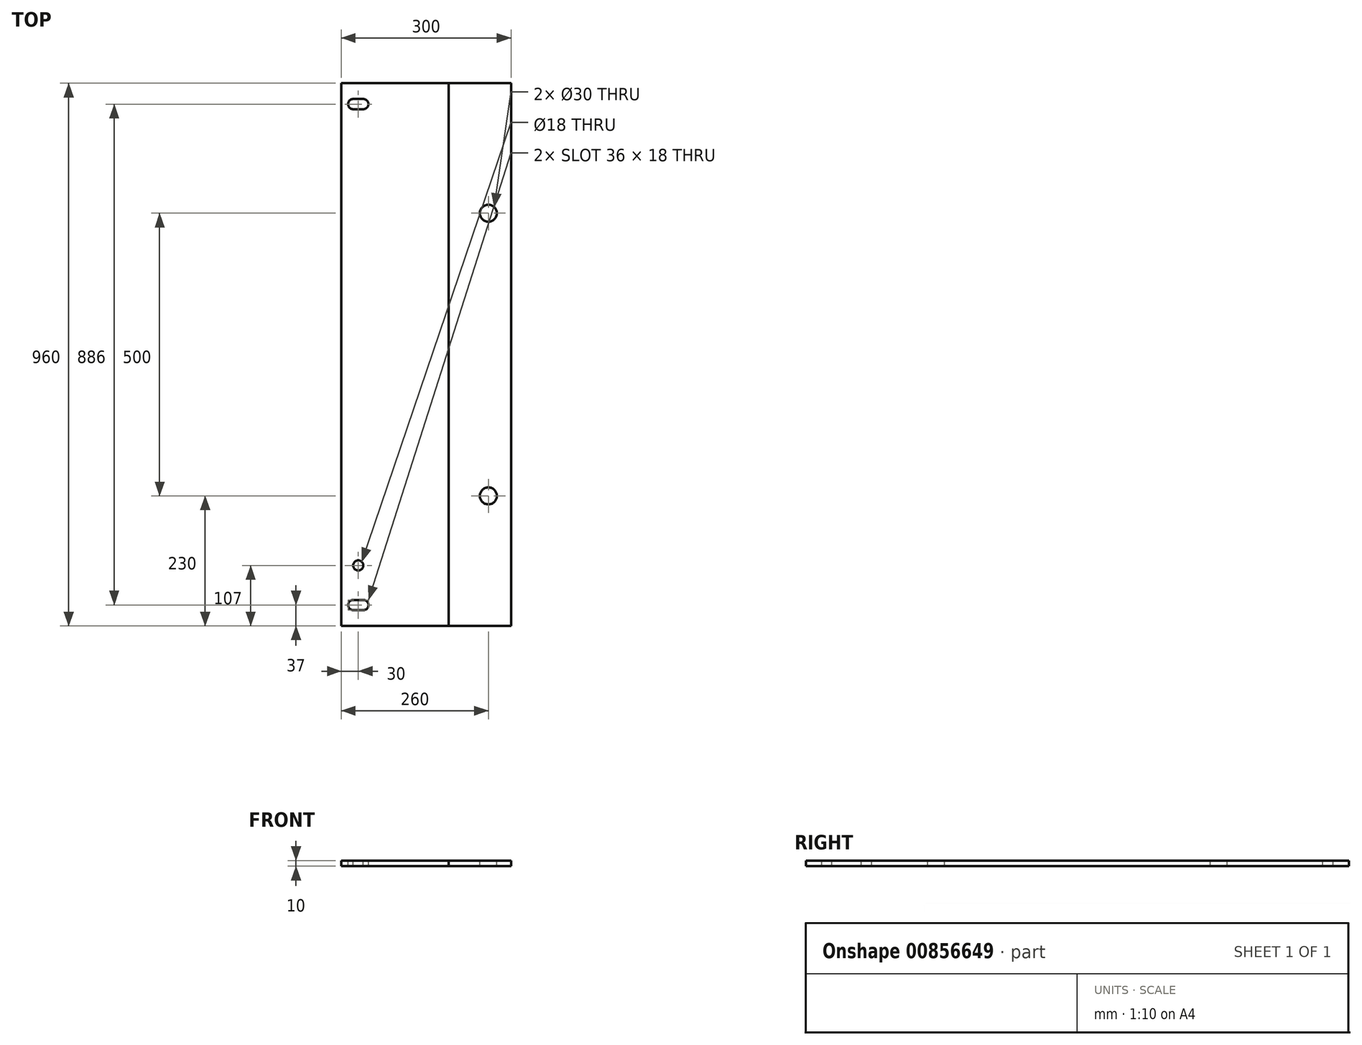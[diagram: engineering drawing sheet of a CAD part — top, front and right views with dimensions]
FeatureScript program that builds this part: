
annotation { "Feature Type Name" : "Feature", "Feature Type Description" : "" }
export const myFeature = defineFeature(function(context is Context, id is Id, definition is map)
    precondition{}
    {
        {
            var Q0;
            Q0=qCreatedBy(makeId("Top.planeOp"),FACE);
            var sketch = newSketch(context, id + "F0", { "sketchPlane" : qUnion([Q0])});
            skLineSegment(sketch, "E0.bottom", {"start": v(95, 480) * mm, "end": v(-95, 480) * mm});
            skLineSegment(sketch, "E0.top", {"start": v(95, -480) * mm, "end": v(-95, -480) * mm});
            skLineSegment(sketch, "E0.left", {"start": v(95, 480) * mm, "end": v(95, -480) * mm});
            skLineSegment(sketch, "E0.right", {"start": v(-95, 480) * mm, "end": v(-95, -480) * mm});
            skPoint(sketch, "E0.middle", {"position": v(0, 0) * mm});
            skLineSegment(sketch, "E1.bottom", {"start": v(95, 480) * mm, "end": v(205, 480) * mm});
            skLineSegment(sketch, "E1.top", {"start": v(95, -480) * mm, "end": v(205, -480) * mm});
            skLineSegment(sketch, "E1.right", {"start": v(205, 480) * mm, "end": v(205, -480) * mm});
            skSolve(sketch);
        }
        {
            var Q0;
            Q0=makeQuery(id+"F0.imprint","IMPRINT",FACE,{"disambiguationData":[TD([[makeQuery(id+"F0.imprint","IMPRINT",EDGE,{"derivedFrom":sQuery(id+"F0.wireOp",EDGE,"E0.bottom")}),1.0]])]});
            extrude(context, id + "F1", {"entities" : qUnion([Q0]), "depth" : 10 * mm, "offsetDistance" : 25 * mm});
        }
        {
            var Q0;
            Q0=makeQuery(id+"F0.imprint","IMPRINT",FACE,{"disambiguationData":[TD([[makeQuery(id+"F0.imprint","IMPRINT",EDGE,{"derivedFrom":sQuery(id+"F0.wireOp",EDGE,"E1.bottom")}),-1.0]])]});
            extrude(context, id + "F2", {"entities" : qUnion([Q0]), "depth" : 10 * mm, "offsetDistance" : 25 * mm});
        }
        {
            var Q0;
            Q0=makeQuery(id+"F1.opExtrude","CAP_FACE",FACE,{"disambiguationData":[OSD([sQuery(id+"F0.wireOp",EDGE,"E0.bottom"),sQuery(id+"F0.wireOp",EDGE,"E0.top"),sQuery(id+"F0.wireOp",EDGE,"E0.right"),sQuery(id+"F0.wireOp",EDGE,"E0.left")])],"isStart":false});
            var sketch = newSketch(context, id + "F3", { "sketchPlane" : qUnion([Q0])});
            skLineSegment(sketch, "E2", {"start": v(-65, -480) * mm, "end": v(-65, 480) * mm, "construction": true});
            skLineSegment(sketch, "E3.bottom", {"start": v(-47, -434) * mm, "end": v(-83, -434) * mm});
            skLineSegment(sketch, "E3.top", {"start": v(-47, -452) * mm, "end": v(-83, -452) * mm});
            skLineSegment(sketch, "E3.left", {"start": v(-47, -434) * mm, "end": v(-47, -452) * mm});
            skLineSegment(sketch, "E3.right", {"start": v(-83, -434) * mm, "end": v(-83, -452) * mm});
            skPoint(sketch, "E3.middle", {"position": v(-65, -443) * mm});
            skLineSegment(sketch, "E4", {"start": v(-74, -452) * mm, "end": v(-74, -434) * mm, "construction": true});
            skArc(sketch, "E5", {"start": v(-74, -434) * mm, "mid": v(-83, -443) * mm, "end": v(-74, -452) * mm});
            skArc(sketch, "E6.MirrorCS", {"start": v(-56, -434) * mm, "mid": v(-47, -443) * mm, "end": v(-56, -452) * mm});
            skLineSegment(sketch, "E7.MirrorCS", {"start": v(-47, 452) * mm, "end": v(-83, 452) * mm});
            skLineSegment(sketch, "E8.MirrorCS", {"start": v(-47, 434) * mm, "end": v(-83, 434) * mm});
            skLineSegment(sketch, "E9.MirrorCS", {"start": v(-47, 434) * mm, "end": v(-47, 452) * mm});
            skArc(sketch, "E10.MirrorCS", {"start": v(-56, 434) * mm, "mid": v(-47, 443) * mm, "end": v(-56, 452) * mm});
            skArc(sketch, "E11.MirrorCS", {"start": v(-74, 434) * mm, "mid": v(-83, 443) * mm, "end": v(-74, 452) * mm});
            skLineSegment(sketch, "E12.MirrorCS", {"start": v(-83, 434) * mm, "end": v(-83, 452) * mm});
            skLineSegment(sketch, "E13", {"start": v(-65, -408) * mm, "end": v(-95, -408) * mm, "construction": true});
            skLineSegment(sketch, "E14", {"start": v(165, 480) * mm, "end": v(165, -480) * mm, "construction": true});
            skPoint(sketch, "E15", {"position": v(165, -250) * mm});
            skPoint(sketch, "E16.MirrorP", {"position": v(165, 250) * mm});
            skPoint(sketch, "E17.MirrorP", {"position": v(-65, -373) * mm});
            skCircle(sketch, "E18", {"center": v(-65, -373) * mm, "radius": 9 * mm});
            skSolve(sketch);
        }
        {
            var Q0;
            {var subQ0=sQuery(id+"F3.wireOp",EDGE,"E5");var subQ1=sQuery(id+"F3.wireOp",EDGE,"E3.bottom");var subQ2=makeQuery(id+"F3.imprint","INTERSECT",VERTEX,{"derivedFrom":[subQ1,subQ0]});Q0=makeQuery(id+"F3.imprint","IMPRINT",FACE,{"disambiguationData":[TD([[makeQuery(id+"F3.imprint","IMPRINT",EDGE,{"disambiguationData":[TD([[subQ2,1.0]])],"derivedFrom":subQ1}),1.0]])]});}
            var Q1;
            Q1=makeQuery(id+"F3.imprint","IMPRINT",FACE,{"disambiguationData":[TD([[makeQuery(id+"F3.imprint","IMPRINT",EDGE,{"derivedFrom":sQuery(id+"F3.wireOp",EDGE,"E18")}),1.0]])]});
            var Q2;
            {var subQ0=sQuery(id+"F3.wireOp",EDGE,"E10.MirrorCS");var subQ4=sQuery(id+"F3.wireOp",EDGE,"E7.MirrorCS");var subQ5=makeQuery(id+"F3.imprint","INTERSECT",VERTEX,{"derivedFrom":[subQ4,subQ0]});Q2=makeQuery(id+"F3.imprint","IMPRINT",FACE,{"disambiguationData":[TD([[makeQuery(id+"F3.imprint","IMPRINT",EDGE,{"disambiguationData":[TD([[subQ5,-1.0]])],"derivedFrom":subQ4}),1.0]])]});}
            extrude(context, id + "F4", {"entities" : qUnion([Q0, Q1, Q2]), "operationType" : NewBodyOperationType.REMOVE, "endBound" : BoundingType.UP_TO_NEXT, "oppositeDirection" : true, "depth" : 25 * mm, "offsetDistance" : 25 * mm});
        }
        {
            var Q0;
            Q0=sQuery(id+"F3.wireOp",VERTEX,"E16.MirrorP");
            var Q1;
            Q1=sQuery(id+"F3.wireOp",VERTEX,"E15");
            var Q2;
            Q2=makeQuery(id+"F2.opExtrude","SWEPT_BODY",BODY,{"disambiguationData":[OSD([sQuery(id+"F0.wireOp",EDGE,"E1.bottom"),sQuery(id+"F0.wireOp",EDGE,"E1.top"),sQuery(id+"F0.wireOp",EDGE,"E0.left"),sQuery(id+"F0.wireOp",EDGE,"E1.right")])]});
            hole(context, id + "F5", {"style" : HoleStyle.SIMPLE, "endStyle" : HoleEndStyle.THROUGH, "holeDiameter" : 30 * mm, "majorDiameter" : 5 * mm, "tappedDepth" : 12 * mm, "tapClearance" : 3, "locations" : qUnion([Q0, Q1]), "scope" : qUnion([Q2])});
        }
    });
